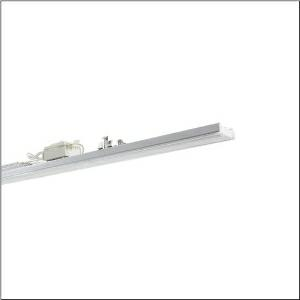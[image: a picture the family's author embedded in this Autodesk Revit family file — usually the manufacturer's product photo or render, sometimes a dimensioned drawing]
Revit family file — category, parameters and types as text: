
# Revit family: licross_r__21_recessed_mo_52te12dn4axg3s4_eb36
name_source: partatom
category: Lighting Fixtures
units: mm (PartAtom-declared; Revit-internal decimal feet)

## family parameters
Cut with Voids When Loaded = No
Host = Face
Light Source = No
Part Type = Normal
Room Calculation Point = No
Round Connector Dimension = Use Diameter
Shared = No

## types (1)
- --- (1 x LED, 950 lm, 6.7 W, 4000K)
    Apparent Load = 7 VA
    CIE Flux Codes = 72 92 99 100 100
    Color Rendering = 80
    Color Temperature = 4000K
    Default Elevation = 1800 mm
    Description = Licross® 21 Recessed MO, luminaire insert, of sheet steel, galvanised, coil coated, white, length: 1.500mm, width: 66mm, height: 67mm, LED rated luminous flux: 10.280lm, light colour: 840, control gear: DALI 2, with plug, 6-pole, with phase selection, for trunking rail, 9 or 11-core, mains connection: 220..240V, AC, 50/60Hz, rated input power: 62W, halogen-free wiring, for emergency light function, for trunking rail, 9-/11-core, converter,control gear: single battery element, battery: LiFePO4, 9Ah, primary optical cover: cover, of PMMA, light emission: direct distribution, primary light characteristic: symmetric, protection rating (complete): IP54, insulation class (complete): insulation class I (protective earthing), certification: CE, UKCA, protection symbol: D if used in an environment with non-conductive dust loads with corresponding accessories, impact resistance: IK06, permissible ambient temperature for indoor applications: +5..+35°C, standard: EN 60598-2-22, LABS conformity tested according to VDMA 24364:2018-05, reducing of maximum allowable ambient temperature of 5°C with ceiling mounting, corresponds to IFS (International Featured Standards) requirements for safety and quality in the food industry, packaging unit: 1 piece
    Height = 58 mm
    Lamp = 1 x LED
    Lamp Light Flux = 950 lm
    Lamp Power = 6.7 W
    Lamp count = 1
    Length = 1500 mm
    Luminous efficacy = 142 lm/W
    Manufacturer = Siteco
    ModVariant = No
    Model = 52TE12DN4AXG3S4
    Mounting Place = Ceiling
    Mounting Type = Pendant
    Number of Poles = 1
    OnlyDefault = Yes
    Power Factor = 1
    Product Name = Licross® 21 Recessed MO
    Product group = luminaire insert
    ProductGroupID = 902
    Protection Class = Protection class I
    Protection Degree = IP 54
    RLX_Detail_Level = 1
    RLX_Emergency_Light_Flux = 0 lm
    RLX_Emergency_Type = 0
    RLX_Emergency_Type_DB = No
    RlxData = <blob elided: 25005 chars, md5=75751967>
    Socket = socket
    Standby Power = 0 W
    System Light Flux = 950 lm
    System Power = 7 W
    Type Comments = : emergency light operation: 3 h
    Type Image = l_1296930.jpg
    URL = http://relux.com
    VarID = @adj_110050
    Voltage = 0 V
    Weight = 0.00 kg
    Width = 66 mm

## geometry (parser evidence)
native form markers: Blend x4, Sweep x10
no freeform markers — native parametric forms only
